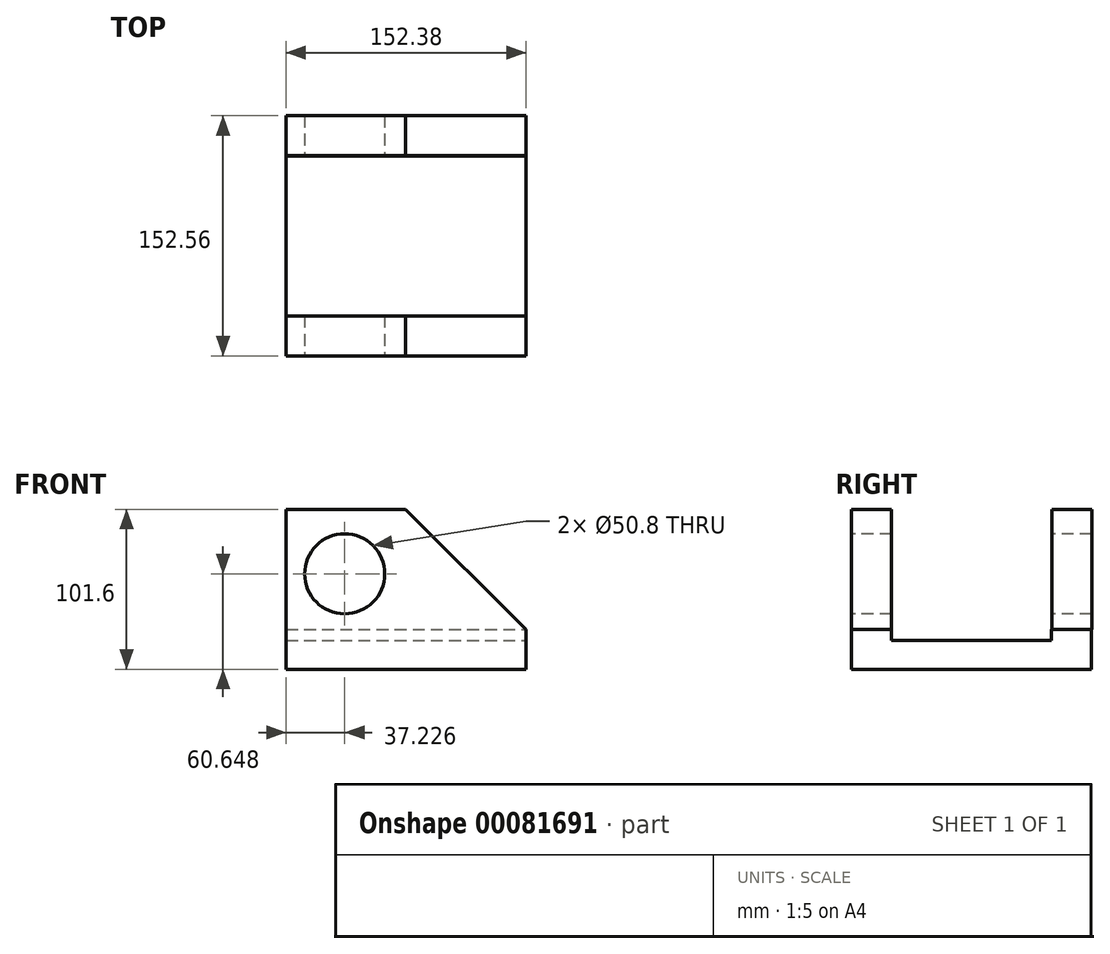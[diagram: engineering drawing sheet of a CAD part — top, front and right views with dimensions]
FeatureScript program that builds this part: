
annotation { "Feature Type Name" : "Feature", "Feature Type Description" : "" }
export const myFeature = defineFeature(function(context is Context, id is Id, definition is map)
    precondition{}
    {
        {
            var Q0;
            Q0=qCreatedBy(makeId("Top.planeOp"),FACE);
            var sketch = newSketch(context, id + "F0", { "sketchPlane" : qUnion([Q0])});
            skLineSegment(sketch, "E0.bottom", {"start": v(76.37, 76.1) * mm, "end": v(-76, 76.1) * mm});
            skLineSegment(sketch, "E0.top", {"start": v(76.37, -76.28) * mm, "end": v(-76, -76.28) * mm});
            skLineSegment(sketch, "E0.left", {"start": v(76.37, 76.1) * mm, "end": v(76.37, -76.28) * mm});
            skLineSegment(sketch, "E0.right", {"start": v(-76, 76.1) * mm, "end": v(-76, -76.28) * mm});
            skSolve(sketch);
        }
        {
            var Q0;
            Q0 = qSketchRegion(id + "F0", true);
            extrude(context, id + "F1", {"entities" : qUnion([Q0]), "oppositeDirection" : true, "depth" : 25.4 * mm});
        }
        {
            var Q0;
            Q0=makeQuery(id+"F1.opExtrude","CAP_FACE",FACE,{"disambiguationData":[OSD([sQuery(id+"F0.wireOp",EDGE,"E0.bottom"),sQuery(id+"F0.wireOp",EDGE,"E0.top"),sQuery(id+"F0.wireOp",EDGE,"E0.left"),sQuery(id+"F0.wireOp",EDGE,"E0.right")])],"isStart":true});
            var sketch = newSketch(context, id + "F2", { "sketchPlane" : qUnion([Q0])});
            skLineSegment(sketch, "E1", {"start": v(-76, -51.1) * mm, "end": v(76.37, -51.1) * mm});
            skLineSegment(sketch, "E2.MirrorCS", {"start": v(-76, 51.1) * mm, "end": v(76.37, 51.1) * mm});
            skSolve(sketch);
        }
        {
            var Q0;
            Q0=makeQuery(id+"F1.opExtrude","SWEPT_FACE",FACE,{"disambiguationData":[OSD([sQuery(id+"F0.wireOp",EDGE,"E0.top")])]});
            var sketch = newSketch(context, id + "F3", { "sketchPlane" : qUnion([Q0])});
            skLineSegment(sketch, "E3.bottom", {"start": v(-76, 0) * mm, "end": v(0, 0) * mm});
            skLineSegment(sketch, "E3.top", {"start": v(-76, 76.2) * mm, "end": v(0, 76.2) * mm});
            skLineSegment(sketch, "E3.left", {"start": v(-76, 0) * mm, "end": v(-76, 76.2) * mm});
            skLineSegment(sketch, "E3.right", {"start": v(0, 0) * mm, "end": v(0, 76.2) * mm});
            skLineSegment(sketch, "E4", {"start": v(0, 76.2) * mm, "end": v(76.37, 0) * mm});
            skPoint(sketch, "E5", {"position": v(-40.2, 37.36) * mm});
            skSolve(sketch);
        }
        {
            var Q0;
            Q0 = qSketchRegion(id + "F3", true);
            extrude(context, id + "F4", {"entities" : qUnion([Q0]), "oppositeDirection" : true, "depth" : 25.4 * mm});
        }
        {
            var Q0;
            Q0=makeQuery(id+"F1.opExtrude","SWEPT_FACE",FACE,{"disambiguationData":[OSD([sQuery(id+"F0.wireOp",EDGE,"E0.top")])]});
            var sketch = newSketch(context, id + "F5", { "sketchPlane" : qUnion([Q0])});
            skLineSegment(sketch, "E6", {"start": v(0, 76.2) * mm, "end": v(76.37, 0) * mm});
            skLineSegment(sketch, "E7", {"start": v(0, 76.2) * mm, "end": v(0, 0) * mm});
            skLineSegment(sketch, "E8", {"start": v(0, 0) * mm, "end": v(76.37, 0) * mm});
            skSolve(sketch);
        }
        {
            var Q0;
            Q0 = qSketchRegion(id + "F5", true);
            extrude(context, id + "F6", {"entities" : qUnion([Q0]), "oppositeDirection" : true, "depth" : 25.4 * mm});
        }
        {
            var Q0;
            Q0=makeQuery(id+"F6.opExtrude","SWEPT_BODY",BODY,{"disambiguationData":[OSD([sQuery(id+"F5.wireOp",EDGE,"E6"),sQuery(id+"F5.wireOp",EDGE,"E7"),sQuery(id+"F5.wireOp",EDGE,"E8")])]});
            var Q1;
            Q1=makeQuery(id+"F4.opExtrude","SWEPT_BODY",BODY,{"disambiguationData":[OSD([sQuery(id+"F3.wireOp",EDGE,"E3.bottom"),sQuery(id+"F3.wireOp",EDGE,"E3.top"),sQuery(id+"F3.wireOp",EDGE,"E3.left"),sQuery(id+"F3.wireOp",EDGE,"E3.right")])]});
            var Q2;
            Q2=qCreatedBy(makeId("Front.planeOp"),FACE);
            mirror(context, id + "F7", {"operationType" : NewBodyOperationType.ADD, "entities" : qUnion([Q0, Q1]), "mirrorPlane" : qUnion([Q2])});
        }
        {
            var Q0;
            Q0=makeQuery(id+"F7.boolean.opBoolean","MERGE",FACE,{"derivedFrom":[makeQuery(id+"F1.opExtrude","SWEPT_FACE",FACE,{"disambiguationData":[OSD([sQuery(id+"F0.wireOp",EDGE,"E0.top")])]}),makeQuery(id+"F4.opExtrude","CAP_FACE",FACE,{"disambiguationData":[OSD([sQuery(id+"F3.wireOp",EDGE,"E3.bottom"),sQuery(id+"F3.wireOp",EDGE,"E3.top"),sQuery(id+"F3.wireOp",EDGE,"E3.left"),sQuery(id+"F3.wireOp",EDGE,"E3.right")])],"isStart":true}),makeQuery(id+"F6.opExtrude","CAP_FACE",FACE,{"disambiguationData":[OSD([sQuery(id+"F5.wireOp",EDGE,"E6"),sQuery(id+"F5.wireOp",EDGE,"E7"),sQuery(id+"F5.wireOp",EDGE,"E8")])],"isStart":true})]});
            var sketch = newSketch(context, id + "F8", { "sketchPlane" : qUnion([Q0])});
            skPoint(sketch, "E9", {"position": v(-38.78, 35.25) * mm});
            skSolve(sketch);
        }
        {
            var Q0;
            Q0=sQuery(id+"F8.wireOp",VERTEX,"E9");
            var Q1;
            Q1=makeQuery(id+"F1.opExtrude","SWEPT_BODY",BODY,{"disambiguationData":[OSD([sQuery(id+"F0.wireOp",EDGE,"E0.bottom"),sQuery(id+"F0.wireOp",EDGE,"E0.top"),sQuery(id+"F0.wireOp",EDGE,"E0.left"),sQuery(id+"F0.wireOp",EDGE,"E0.right")])]});
            hole(context, id + "F9", {"style" : HoleStyle.SIMPLE, "endStyle" : HoleEndStyle.THROUGH, "holeDiameter" : 50.8 * mm, "locations" : qUnion([Q0]), "scope" : qUnion([Q1]), "isTappedThrough" : true});
        }
        {
            var Q0;
            Q0=makeQuery(id+"F1.opExtrude","SWEPT_FACE",FACE,{"disambiguationData":[OSD([sQuery(id+"F0.wireOp",EDGE,"E0.left")])]});
            var sketch = newSketch(context, id + "F10", { "sketchPlane" : qUnion([Q0])});
            skLineSegment(sketch, "E10.bottom", {"start": v(-50.88, 0) * mm, "end": v(50.72, 0) * mm});
            skLineSegment(sketch, "E10.top", {"start": v(-50.88, -7.18) * mm, "end": v(50.72, -7.18) * mm});
            skLineSegment(sketch, "E10.left", {"start": v(-50.88, 0) * mm, "end": v(-50.88, -7.18) * mm});
            skLineSegment(sketch, "E10.right", {"start": v(50.72, 0) * mm, "end": v(50.72, -7.18) * mm});
            skSolve(sketch);
        }
        {
            var Q0;
            Q0 = qSketchRegion(id + "F10", true);
            extrude(context, id + "F11", {"entities" : qUnion([Q0]), "operationType" : NewBodyOperationType.REMOVE, "oppositeDirection" : true, "depth" : 152.4 * mm});
        }
    });
